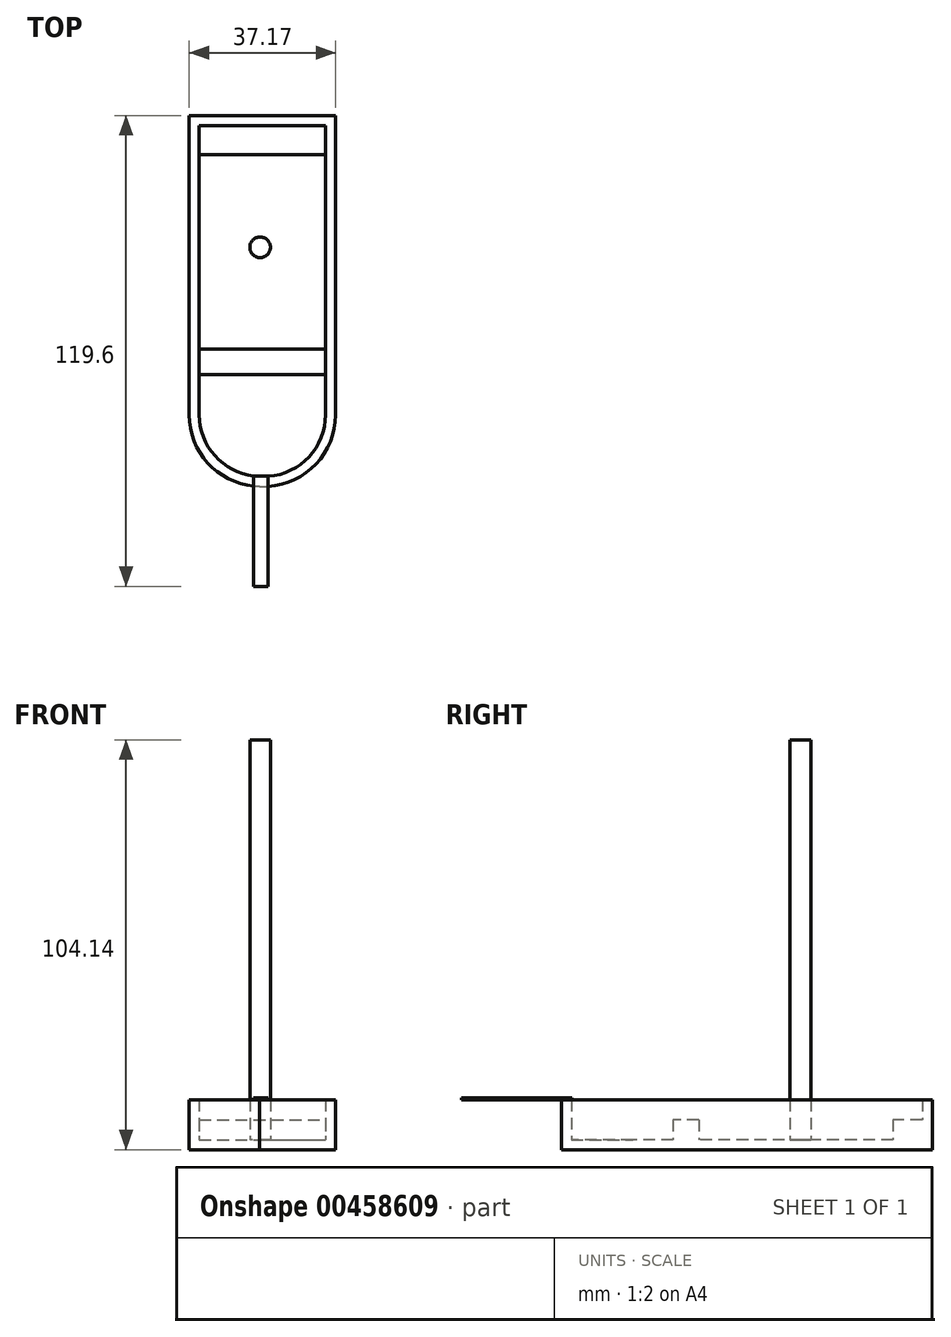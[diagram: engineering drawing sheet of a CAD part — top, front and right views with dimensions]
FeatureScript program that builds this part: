
annotation { "Feature Type Name" : "Feature", "Feature Type Description" : "" }
export const myFeature = defineFeature(function(context is Context, id is Id, definition is map)
    precondition{}
    {
        {
            var Q0;
            Q0=qCreatedBy(makeId("Top.planeOp"),FACE);
            var sketch = newSketch(context, id + "F0", { "sketchPlane" : qUnion([Q0])});
            skLineSegment(sketch, "E0.bottom", {"start": v(0, 76.04) * mm, "end": v(37.17, 76.04) * mm});
            skLineSegment(sketch, "E0.top", {"start": v(0, 0) * mm, "end": v(37.17, 0) * mm});
            skLineSegment(sketch, "E0.left", {"start": v(0, 76.04) * mm, "end": v(0, 0) * mm});
            skLineSegment(sketch, "E0.right", {"start": v(37.17, 76.04) * mm, "end": v(37.17, 0) * mm});
            skArc(sketch, "E1", {"start": v(0, 0) * mm, "mid": v(5.22, -12.74) * mm, "end": v(17.87, -18.16) * mm});
            skArc(sketch, "E2", {"start": v(17.87, -18.16) * mm, "mid": v(31.44, -13.25) * mm, "end": v(37.17, 0) * mm});
            skSolve(sketch);
        }
        {
            var Q0;
            Q0 = qSketchRegion(id + "F0", true);
            extrude(context, id + "F1", {"entities" : qUnion([Q0]), "depth" : 12.7 * mm});
        }
        {
            var Q0;
            Q0=makeQuery(id+"F1.opExtrude","CAP_FACE",FACE,{"disambiguationData":[OSD([sQuery(id+"F0.wireOp",EDGE,"E0.bottom"),sQuery(id+"F0.wireOp",EDGE,"E0.left"),sQuery(id+"F0.wireOp",EDGE,"E0.right"),sQuery(id+"F0.wireOp",EDGE,"E1"),sQuery(id+"F0.wireOp",EDGE,"E2")])],"isStart":false});
            shell(context, id + "F2", {"entities" : qUnion([Q0]), "thickness" : 2.54 * mm});
        }
        {
            var Q0;
            Q0=makeQuery(id+"F2.opShell","OFFSET_FACE",FACE,{"disambiguationData":[OSD([sQuery(id+"F0.wireOp",EDGE,"E0.bottom"),sQuery(id+"F0.wireOp",EDGE,"E0.left"),sQuery(id+"F0.wireOp",EDGE,"E0.right"),sQuery(id+"F0.wireOp",EDGE,"E1"),sQuery(id+"F0.wireOp",EDGE,"E2")])]});
            var sketch = newSketch(context, id + "F3", { "sketchPlane" : qUnion([Q0])});
            skLineSegment(sketch, "E3.bottom", {"start": v(2.54, 73.5) * mm, "end": v(34.63, 73.5) * mm});
            skLineSegment(sketch, "E3.top", {"start": v(2.54, 66.1) * mm, "end": v(34.63, 66.1) * mm});
            skLineSegment(sketch, "E3.left", {"start": v(2.54, 73.5) * mm, "end": v(2.54, 66.1) * mm});
            skLineSegment(sketch, "E3.right", {"start": v(34.63, 73.5) * mm, "end": v(34.63, 66.1) * mm});
            skLineSegment(sketch, "E4.bottom", {"start": v(2.54, 10.21) * mm, "end": v(34.63, 10.21) * mm});
            skLineSegment(sketch, "E4.top", {"start": v(2.54, 16.74) * mm, "end": v(34.63, 16.74) * mm});
            skLineSegment(sketch, "E4.left", {"start": v(2.54, 10.21) * mm, "end": v(2.54, 16.74) * mm});
            skLineSegment(sketch, "E4.right", {"start": v(34.63, 10.21) * mm, "end": v(34.63, 16.74) * mm});
            skSolve(sketch);
        }
        {
            var Q0;
            Q0 = qSketchRegion(id + "F3", true);
            extrude(context, id + "F4", {"entities" : qUnion([Q0]), "operationType" : NewBodyOperationType.ADD, "depth" : 5.08 * mm});
        }
        {
            var Q0;
            {var subQ0=sQuery(id+"F0.wireOp",EDGE,"E0.left");var subQ1=sQuery(id+"F0.wireOp",EDGE,"E0.right");Q0=makeQuery(id+"F4.boolean.opBoolean","SPLIT",FACE,{"disambiguationData":[TD([makeQuery(id+"F4.opExtrude","SWEPT_FACE",FACE,{"disambiguationData":[OSD([sQuery(id+"F3.wireOp",EDGE,"E3.top")])]})])],"derivedFrom":makeQuery(id+"F2.opShell","OFFSET_FACE",FACE,{"disambiguationData":[OSD([sQuery(id+"F0.wireOp",EDGE,"E0.bottom"),subQ0,subQ1,sQuery(id+"F0.wireOp",EDGE,"E1"),sQuery(id+"F0.wireOp",EDGE,"E2")])]})});}
            var sketch = newSketch(context, id + "F5", { "sketchPlane" : qUnion([Q0])});
            skCircle(sketch, "E5", {"center": v(18.02, 42.56) * mm, "radius": 2.62 * mm});
            skSolve(sketch);
        }
        {
            var Q0;
            Q0 = qSketchRegion(id + "F5", true);
            extrude(context, id + "F6", {"entities" : qUnion([Q0]), "operationType" : NewBodyOperationType.ADD, "depth" : 101.6 * mm});
        }
        {
            var Q0;
            Q0=makeQuery(id+"F1.opExtrude","CAP_FACE",FACE,{"disambiguationData":[OSD([sQuery(id+"F0.wireOp",EDGE,"E0.bottom"),sQuery(id+"F0.wireOp",EDGE,"E0.left"),sQuery(id+"F0.wireOp",EDGE,"E0.right"),sQuery(id+"F0.wireOp",EDGE,"E1"),sQuery(id+"F0.wireOp",EDGE,"E2")])],"isStart":false});
            var sketch = newSketch(context, id + "F7", { "sketchPlane" : qUnion([Q0])});
            skLineSegment(sketch, "E6.bottom", {"start": v(16.4, -15.52) * mm, "end": v(20.08, -15.52) * mm});
            skLineSegment(sketch, "E6.top", {"start": v(16.4, -18.16) * mm, "end": v(20.08, -18.16) * mm});
            skLineSegment(sketch, "E6.left", {"start": v(16.4, -15.52) * mm, "end": v(16.4, -18.16) * mm});
            skLineSegment(sketch, "E6.right", {"start": v(20.08, -15.52) * mm, "end": v(20.08, -18.16) * mm});
            skSolve(sketch);
        }
        {
            var Q0;
            Q0 = qSketchRegion(id + "F7", true);
            extrude(context, id + "F8", {"entities" : qUnion([Q0]), "operationType" : NewBodyOperationType.ADD, "depth" : 0.5 * mm});
        }
        {
            var Q0;
            Q0=makeQuery(id+"F8.opExtrude","SWEPT_FACE",FACE,{"disambiguationData":[OSD([sQuery(id+"F7.wireOp",EDGE,"E6.top")])]});
            extrude(context, id + "F9", {"entities" : qUnion([Q0]), "operationType" : NewBodyOperationType.ADD, "depth" : 25.4 * mm});
        }
    });
